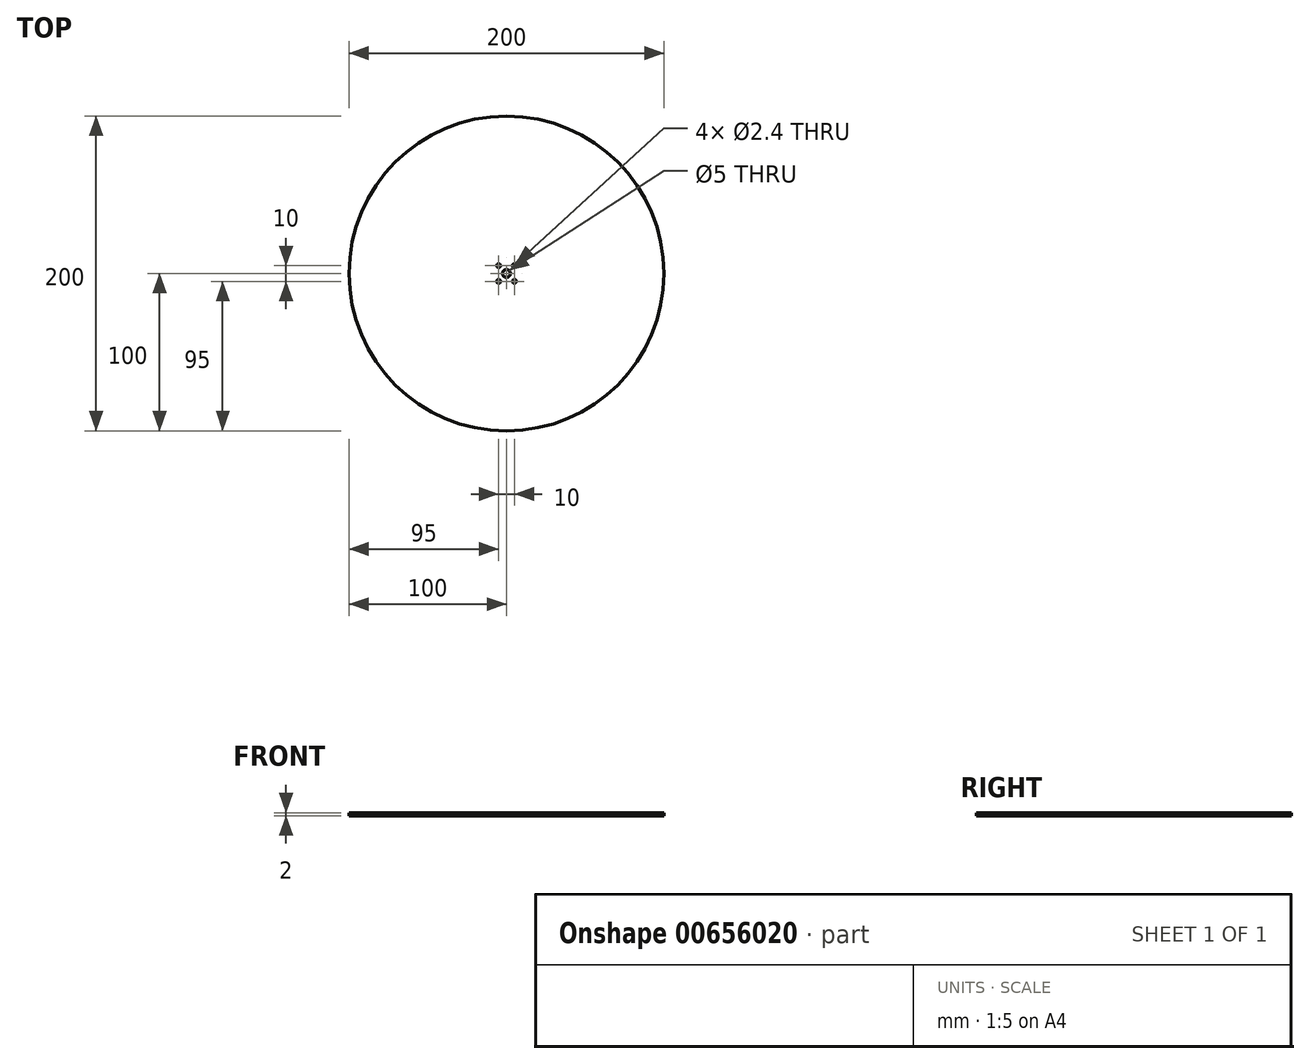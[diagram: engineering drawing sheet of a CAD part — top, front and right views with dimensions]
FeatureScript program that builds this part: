
annotation { "Feature Type Name" : "Feature", "Feature Type Description" : "" }
export const myFeature = defineFeature(function(context is Context, id is Id, definition is map)
    precondition{}
    {
        {
            var Q0;
            Q0=qCreatedBy(makeId("Top.planeOp"),FACE);
            var sketch = newSketch(context, id + "F0", { "sketchPlane" : qUnion([Q0])});
            skCircle(sketch, "E0", {"center": v(0, 0) * mm, "radius": 100 * mm});
            skCircle(sketch, "E1", {"center": v(0, 0) * mm, "radius": 2.5 * mm});
            skCircle(sketch, "E2", {"center": v(-5, 5) * mm, "radius": 1.2 * mm});
            skCircle(sketch, "E3", {"center": v(5, 5) * mm, "radius": 1.2 * mm});
            skCircle(sketch, "E4", {"center": v(-5, -5) * mm, "radius": 1.2 * mm});
            skCircle(sketch, "E5", {"center": v(5, -5) * mm, "radius": 1.2 * mm});
            skSolve(sketch);
        }
        {
            var Q0;
            Q0=makeQuery(id+"F0.imprint","IMPRINT",FACE,{"disambiguationData":[TD([[makeQuery(id+"F0.imprint","IMPRINT",EDGE,{"derivedFrom":sQuery(id+"F0.wireOp",EDGE,"E0")}),1.0]])]});
            extrude(context, id + "F1", {"entities" : qUnion([Q0]), "depth" : 2 * mm, "offsetDistance" : 25 * mm});
        }
    });
